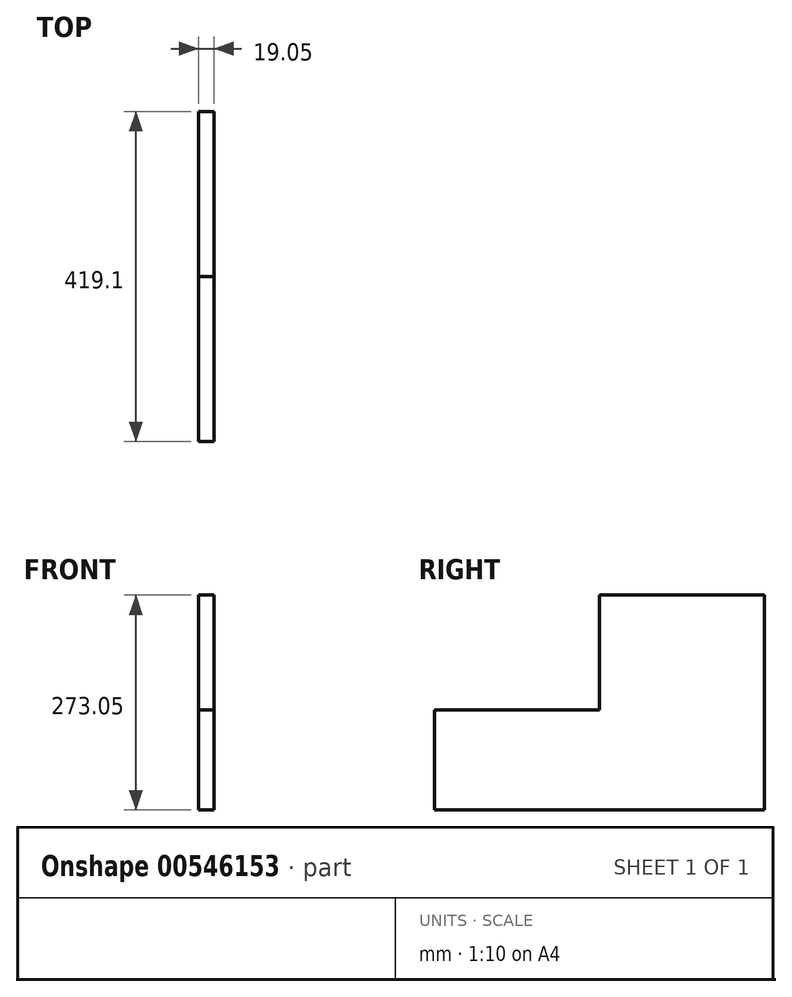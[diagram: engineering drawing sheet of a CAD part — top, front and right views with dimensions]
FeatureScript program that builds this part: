
annotation { "Feature Type Name" : "Feature", "Feature Type Description" : "" }
export const myFeature = defineFeature(function(context is Context, id is Id, definition is map)
    precondition{}
    {
        {
            var Q0;
            Q0=qCreatedBy(makeId("Right.planeOp"),FACE);
            var sketch = newSketch(context, id + "F0", { "sketchPlane" : qUnion([Q0])});
            skLineSegment(sketch, "E0.bottom", {"start": v(0, 0) * mm, "end": v(209.55, 0) * mm});
            skLineSegment(sketch, "E0.top", {"start": v(0, 146.05) * mm, "end": v(209.55, 146.05) * mm});
            skLineSegment(sketch, "E0.left", {"start": v(0, 0) * mm, "end": v(0, 146.05) * mm});
            skLineSegment(sketch, "E0.right", {"start": v(209.55, 0) * mm, "end": v(209.55, 146.05) * mm});
            skLineSegment(sketch, "E1.bottom", {"start": v(-209.55, 0) * mm, "end": v(209.55, 0) * mm});
            skLineSegment(sketch, "E1.top", {"start": v(-209.55, -127) * mm, "end": v(209.55, -127) * mm});
            skLineSegment(sketch, "E1.left", {"start": v(-209.55, 0) * mm, "end": v(-209.55, -127) * mm});
            skLineSegment(sketch, "E1.right", {"start": v(209.55, 0) * mm, "end": v(209.55, -127) * mm});
            skSolve(sketch);
        }
        {
            var Q0;
            Q0=makeQuery(id+"F0.imprint","IMPRINT",FACE,{"disambiguationData":[TD([[makeQuery(id+"F0.imprint","IMPRINT",EDGE,{"derivedFrom":sQuery(id+"F0.wireOp",EDGE,"E0.top")}),-1.0]])]});
            var Q1;
            Q1=makeQuery(id+"F0.imprint","IMPRINT",FACE,{"disambiguationData":[TD([[makeQuery(id+"F0.imprint","IMPRINT",EDGE,{"derivedFrom":sQuery(id+"F0.wireOp",EDGE,"E1.top")}),1.0]])]});
            extrude(context, id + "F1", {"entities" : qUnion([Q0, Q1]), "depth" : 19.05 * mm, "offsetDistance" : 25.4 * mm});
        }
    });
